# Revit family: BC_Hitachi_RPF-FSN2E-1.0-2.5_LOD400
name_source: partatom
category: Equipement de génie climatique
revit_build: Autodesk Revit 2016 (Build: 20150220_1215(x64)
units: mm (PartAtom-declared; Revit-internal decimal feet)

## family parameters
Cote de connecteur circulaire = Utiliser le diamètre
Couper avec des vides une fois chargée = Non
Hôte = Face
Numéro OmniClass = 23.75.00.00
Partagée = Non
Point de calcul de pièce = Non
Titre OmniClass = Climate Control (HVAC)
Type d'élément = Normal

## types (4) — shared parameters
Color = Spring white (4.1Y8.5/0.7)
Description = RPF - FSN2E - Floor type
Elévation par défaut = 1219.20 mm
Fabricant = HITACHI
Frequency = 50 Hz
Maximum AC Voltage = 253 V
Minimum AC Voltage = 207 V
Modèle = RPF - FSN2E - Floor type
Nominal Voltage = 230 V
Number of Poles = 1
Outlet Diameter = 20.00 mm
Overall Depth = 220.00 mm
Overall Height = 630.00 mm
Refrigerant = R410A (factory-charged corrosion-proof nitrogen)
Usage Current = 5 A
Void width = 157.00 mm

## per-type parameters (varying)
| type | Acoustic Pressure Level Maxi (dB) | Acoustic Pressure Level Medium (dB) | Acoustic Pressure Level Mini (dB) | Air Flow (HiH/Hi/Me/low) m3/min | Cooling Capacity | Fan motor input | Gas Diameter | Heating Capacity | Liquid Diameter | Mass | Maximum Air Flow | Minimum Air Flow | Overall Width | Product Code | Sound power max (dB(A)) |
| RPF FSN2E 1.0 | 35 | 32 | 29 | 8.5/7/6 | 3 kW | 20 W | 12.70 mm | 3 kW | 6.35 mm | 25.00 kg | 8500.0 L/min | 6000.0 L/min | 1045.00 mm | 7E450001 | 57 |
| RPF FSN2E 2.5 | 42 | 38 | 34 | 16/14/11 | 6 kW | 45 W | 15.88 mm | 6 kW | 9.52 mm | 34.00 kg | 16000.0 L/min | 11000.0 L/min | 1420.00 mm | 7E450004 | 60 |
| RPF FSN2E 2.0 | 39 | 36 | 32 | 16/14/11 | 5 kW | 45 W | 12.70 mm | 6 kW | 6.35 mm | 33.00 kg | 16000.0 L/min | 11000.0 L/min | 1420.00 mm | 7E450003 | 60 |
| RPF FSN2E 1.5 | 38 | 35 | 31 | 8.5/7/6 | 4 kW | 28 W | 12.70 mm | 4 kW | 6.35 mm | 28.00 kg | 8500.0 L/min | 6000.0 L/min | 1170.00 mm | 7E450002 | 60 |

note: column(s) folded — value = type name in every type: Commentaires du type

## geometry (parser evidence)
native form markers: Blend x2
no freeform markers — native parametric forms only
